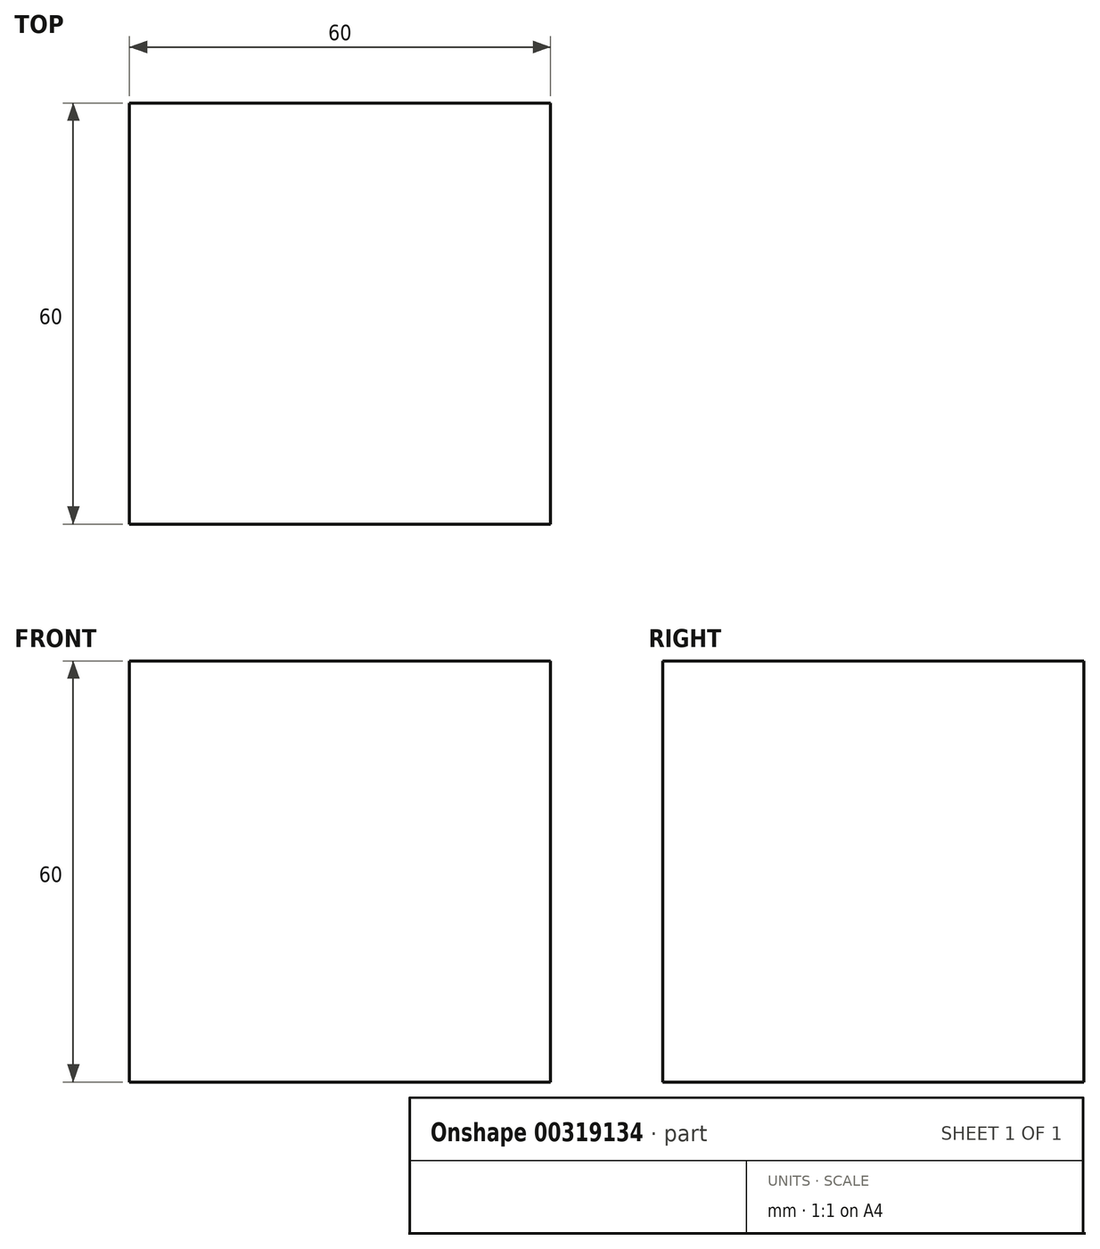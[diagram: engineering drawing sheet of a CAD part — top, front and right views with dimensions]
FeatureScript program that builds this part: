
annotation { "Feature Type Name" : "Feature", "Feature Type Description" : "" }
export const myFeature = defineFeature(function(context is Context, id is Id, definition is map)
    precondition{}
    {
        {
            var Q0;
            Q0=qCreatedBy(makeId("Front.planeOp"),FACE);
            var sketch = newSketch(context, id + "F0", { "sketchPlane" : qUnion([Q0])});
            skLineSegment(sketch, "E0.bottom", {"start": v(0, 0) * mm, "end": v(60, 0) * mm});
            skLineSegment(sketch, "E0.top", {"start": v(0, 60) * mm, "end": v(60, 60) * mm});
            skLineSegment(sketch, "E0.left", {"start": v(0, 0) * mm, "end": v(0, 60) * mm});
            skLineSegment(sketch, "E0.right", {"start": v(60, 0) * mm, "end": v(60, 60) * mm});
            skPoint(sketch, "E1.top.end.orphan", {"position": v(107.04, 60) * mm});
            skSolve(sketch);
        }
        {
            var Q0;
            Q0=makeQuery(id+"F0.imprint","IMPRINT",FACE,{"disambiguationData":[TD([[makeQuery(id+"F0.imprint","IMPRINT",EDGE,{"derivedFrom":sQuery(id+"F0.wireOp",EDGE,"E0.bottom")}),1.0]])]});
            extrude(context, id + "F1", {"entities" : qUnion([Q0]), "depth" : 60 * mm});
        }
    });
